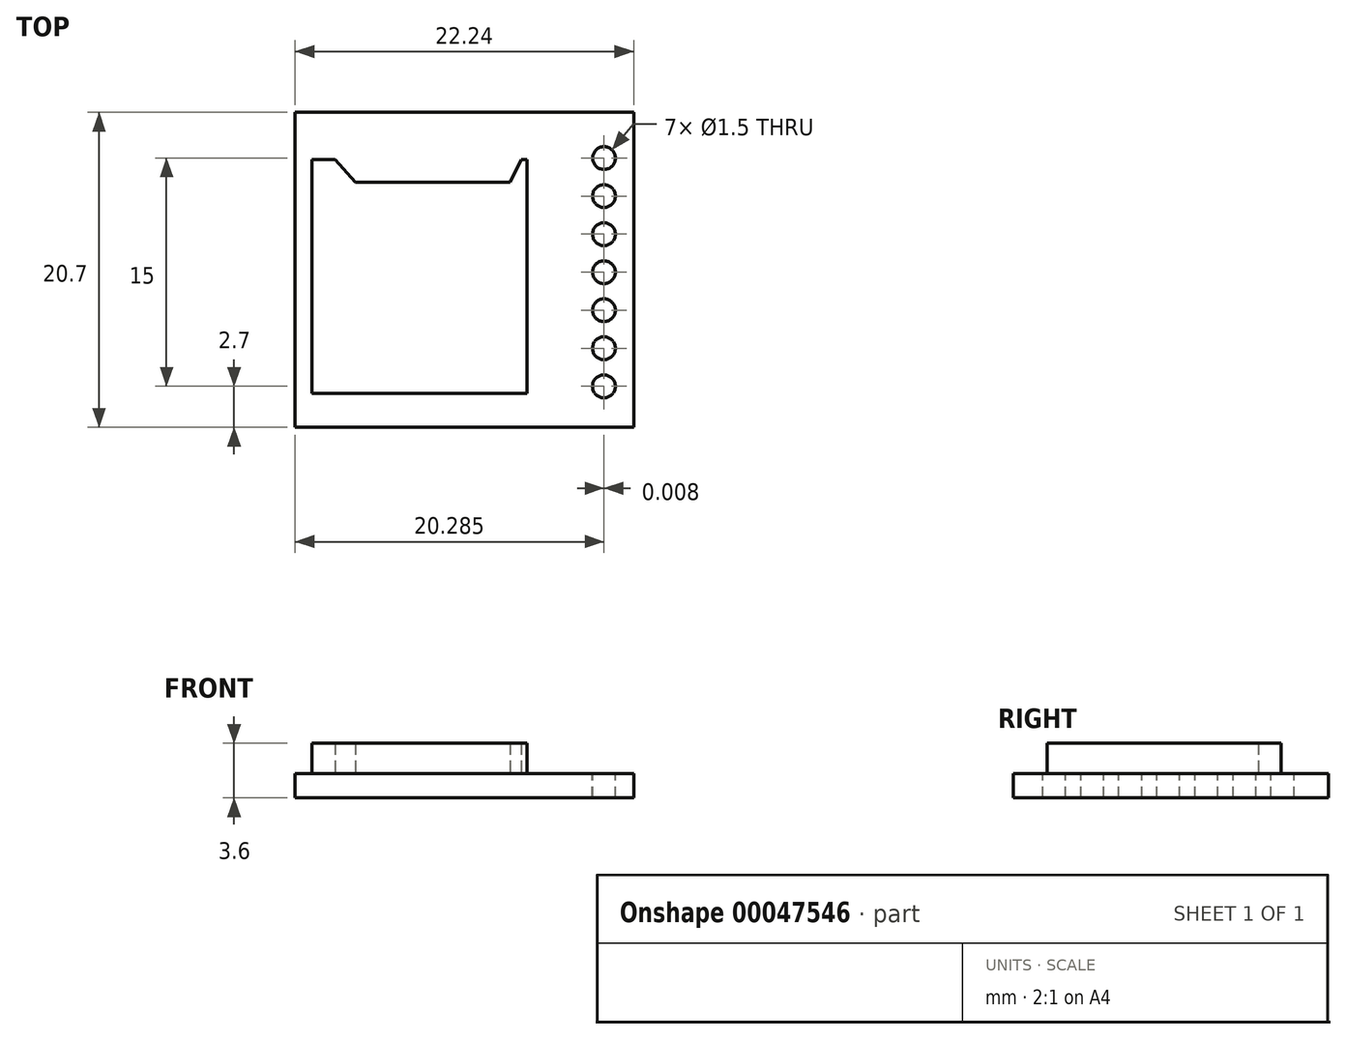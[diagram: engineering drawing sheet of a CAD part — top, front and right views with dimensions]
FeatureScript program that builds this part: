
annotation { "Feature Type Name" : "Feature", "Feature Type Description" : "" }
export const myFeature = defineFeature(function(context is Context, id is Id, definition is map)
    precondition{}
    {
        {
            var Q0;
            Q0=qCreatedBy(makeId("Top.planeOp"),FACE);
            var sketch = newSketch(context, id + "F0", { "sketchPlane" : qUnion([Q0])});
            skLineSegment(sketch, "E0.bottom", {"start": v(-11.12, 10.35) * mm, "end": v(11.13, 10.35) * mm});
            skLineSegment(sketch, "E0.top", {"start": v(-11.12, -10.35) * mm, "end": v(11.13, -10.35) * mm});
            skLineSegment(sketch, "E0.left", {"start": v(-11.12, 10.35) * mm, "end": v(-11.12, -10.35) * mm});
            skLineSegment(sketch, "E0.right", {"start": v(11.13, 10.35) * mm, "end": v(11.13, -10.35) * mm});
            skSolve(sketch);
        }
        {
            var Q0;
            Q0 = qSketchRegion(id + "F0", true);
            extrude(context, id + "F1", {"entities" : qUnion([Q0]), "depth" : 1.6 * mm});
        }
        {
            var Q0;
            Q0=makeQuery(id+"F1.opExtrude","CAP_FACE",FACE,{"disambiguationData":[OSD([sQuery(id+"F0.wireOp",EDGE,"E0.bottom"),sQuery(id+"F0.wireOp",EDGE,"E0.top"),sQuery(id+"F0.wireOp",EDGE,"E0.left"),sQuery(id+"F0.wireOp",EDGE,"E0.right")])],"isStart":false});
            var sketch = newSketch(context, id + "F2", { "sketchPlane" : qUnion([Q0])});
            skLineSegment(sketch, "E1.bottom", {"start": v(-10.02, 7.25) * mm, "end": v(-8.5, 7.25) * mm});
            skLineSegment(sketch, "E1.top", {"start": v(-10.02, -8.1) * mm, "end": v(4.13, -8.1) * mm});
            skLineSegment(sketch, "E1.left", {"start": v(-10.02, 7.25) * mm, "end": v(-10.02, -8.1) * mm});
            skLineSegment(sketch, "E1.right", {"start": v(4.13, 7.25) * mm, "end": v(4.13, -8.1) * mm});
            skLineSegment(sketch, "E2", {"start": v(-17.05, 5.75) * mm, "end": v(-10.02, 5.75) * mm});
            skLineSegment(sketch, "E3", {"start": v(-8.5, 7.25) * mm, "end": v(-7.15, 5.75) * mm});
            skLineSegment(sketch, "E4", {"start": v(3.74, 7.25) * mm, "end": v(3.02, 5.75) * mm});
            skLineSegment(sketch, "E5.trimOffspring", {"start": v(3.74, 7.25) * mm, "end": v(4.13, 7.25) * mm});
            skLineSegment(sketch, "E6.trimOffspring", {"start": v(4.13, 5.75) * mm, "end": v(11.13, 5.75) * mm});
            skLineSegment(sketch, "E7.trimOffspring", {"start": v(-7.15, 5.75) * mm, "end": v(3.02, 5.75) * mm});
            skSolve(sketch);
        }
        {
            var Q0;
            Q0 = qSketchRegion(id + "F2", true);
            extrude(context, id + "F3", {"entities" : qUnion([Q0]), "operationType" : NewBodyOperationType.ADD, "depth" : 2 * mm});
        }
        {
            var Q0;
            Q0=makeQuery(id+"F1.opExtrude","CAP_FACE",FACE,{"disambiguationData":[OSD([sQuery(id+"F0.wireOp",EDGE,"E0.bottom"),sQuery(id+"F0.wireOp",EDGE,"E0.top"),sQuery(id+"F0.wireOp",EDGE,"E0.left"),sQuery(id+"F0.wireOp",EDGE,"E0.right")])],"isStart":false});
            var sketch = newSketch(context, id + "F4", { "sketchPlane" : qUnion([Q0])});
            skCircle(sketch, "E8", {"center": v(9.17, 7.35) * mm, "radius": 0.75 * mm});
            skCircle(sketch, "E9.1.0.0", {"center": v(9.17, 4.85) * mm, "radius": 0.75 * mm});
            skCircle(sketch, "E9.2.0.0", {"center": v(9.17, 2.35) * mm, "radius": 0.75 * mm});
            skCircle(sketch, "E9.3.0.0", {"center": v(9.17, -0.15) * mm, "radius": 0.75 * mm});
            skCircle(sketch, "E9.4.0.0", {"center": v(9.17, -2.65) * mm, "radius": 0.75 * mm});
            skCircle(sketch, "E9.5.0.0", {"center": v(9.17, -5.15) * mm, "radius": 0.75 * mm});
            skCircle(sketch, "E9.6.0.0", {"center": v(9.16, -7.65) * mm, "radius": 0.75 * mm});
            skLineSegment(sketch, "E9.direction1", {"start": v(9.17, 7.35) * mm, "end": v(9.17, 4.85) * mm, "construction": true});
            skSolve(sketch);
        }
        {
            var Q0;
            Q0 = qSketchRegion(id + "F4", true);
            extrude(context, id + "F5", {"entities" : qUnion([Q0]), "operationType" : NewBodyOperationType.REMOVE, "oppositeDirection" : true, "depth" : 25 * mm});
        }
    });
